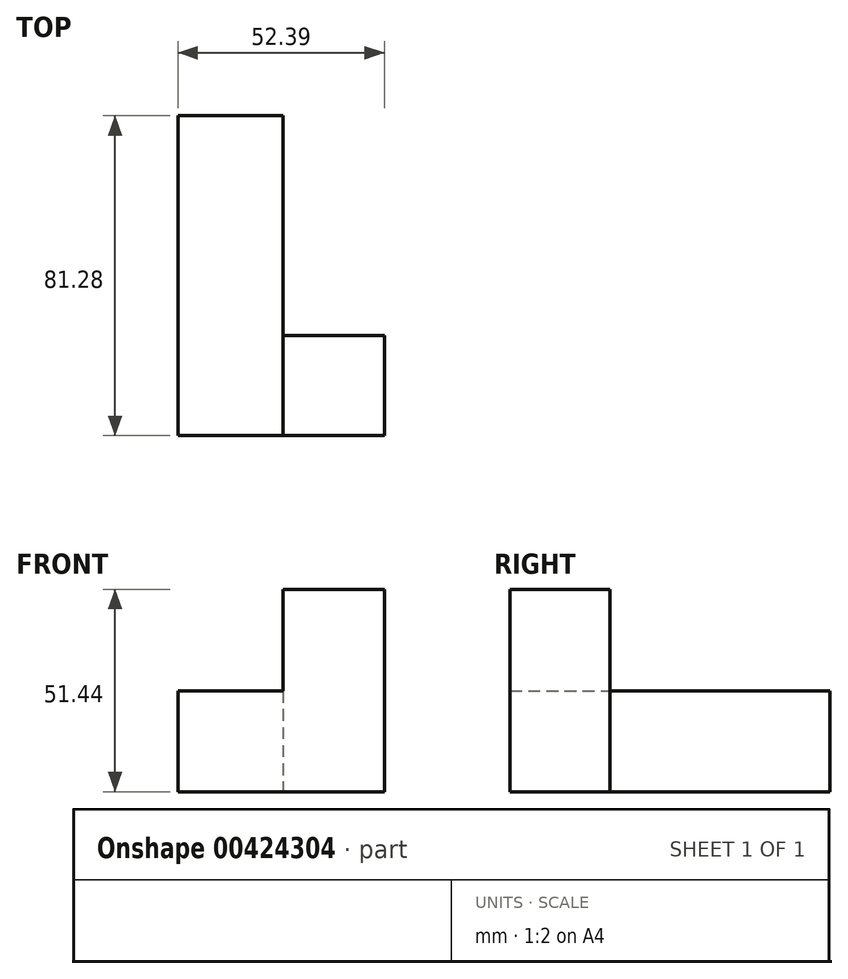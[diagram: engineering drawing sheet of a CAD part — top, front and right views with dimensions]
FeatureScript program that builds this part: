
annotation { "Feature Type Name" : "Feature", "Feature Type Description" : "" }
export const myFeature = defineFeature(function(context is Context, id is Id, definition is map)
    precondition{}
    {
        {
            var Q0;
            Q0=qCreatedBy(makeId("Front.planeOp"),FACE);
            var sketch = newSketch(context, id + "F0", { "sketchPlane" : qUnion([Q0])});
            skLineSegment(sketch, "E0.bottom", {"start": v(0, 0) * mm, "end": v(-25.72, 0) * mm});
            skLineSegment(sketch, "E0.top", {"start": v(0, -25.85) * mm, "end": v(-25.72, -25.85) * mm});
            skLineSegment(sketch, "E0.left", {"start": v(0, 0) * mm, "end": v(0, -25.85) * mm});
            skLineSegment(sketch, "E0.right", {"start": v(-25.72, 0) * mm, "end": v(-25.72, -25.85) * mm});
            skLineSegment(sketch, "E1.top", {"start": v(0, -51.44) * mm, "end": v(-25.72, -51.44) * mm});
            skLineSegment(sketch, "E1.left", {"start": v(0, -25.85) * mm, "end": v(0, -51.44) * mm});
            skLineSegment(sketch, "E1.right", {"start": v(-25.72, -25.85) * mm, "end": v(-25.72, -51.44) * mm});
            skLineSegment(sketch, "E2.bottom", {"start": v(-25.72, -51.44) * mm, "end": v(-52.39, -51.44) * mm});
            skLineSegment(sketch, "E2.top", {"start": v(-25.72, -25.85) * mm, "end": v(-52.39, -25.85) * mm});
            skLineSegment(sketch, "E2.left", {"start": v(-25.72, -51.44) * mm, "end": v(-25.72, -25.85) * mm});
            skLineSegment(sketch, "E2.right", {"start": v(-52.39, -51.44) * mm, "end": v(-52.39, -25.85) * mm});
            skSolve(sketch);
        }
        {
            var Q0;
            Q0=makeQuery(id+"F0.imprint","IMPRINT",FACE,{"disambiguationData":[TD([[makeQuery(id+"F0.imprint","IMPRINT",EDGE,{"derivedFrom":sQuery(id+"F0.wireOp",EDGE,"E0.bottom")}),1.0]])]});
            extrude(context, id + "F1", {"entities" : qUnion([Q0]), "depth" : 25.4 * mm});
        }
        {
            var Q0;
            Q0=makeQuery(id+"F0.imprint","IMPRINT",FACE,{"disambiguationData":[TD([[makeQuery(id+"F0.imprint","IMPRINT",EDGE,{"derivedFrom":sQuery(id+"F0.wireOp",EDGE,"E2.bottom")}),-1.0]])]});
            extrude(context, id + "F2", {"entities" : qUnion([Q0]), "depth" : 25.4 * mm});
        }
        {
            var Q0;
            Q0=makeQuery(id+"F0.imprint","IMPRINT",FACE,{"disambiguationData":[TD([[makeQuery(id+"F0.imprint","IMPRINT",EDGE,{"derivedFrom":sQuery(id+"F0.wireOp",EDGE,"E0.top")}),1.0]])]});
            extrude(context, id + "F3", {"entities" : qUnion([Q0]), "depth" : 25.4 * mm});
        }
        {
            var Q0;
            Q0=makeQuery(id+"F0.imprint","IMPRINT",FACE,{"disambiguationData":[TD([[makeQuery(id+"F0.imprint","IMPRINT",EDGE,{"derivedFrom":sQuery(id+"F0.wireOp",EDGE,"E0.top")}),1.0]])]});
            extrude(context, id + "F4", {"entities" : qUnion([Q0]), "depth" : 25.4 * mm});
        }
        {
            var Q0;
            Q0=makeQuery(id+"F0.imprint","IMPRINT",FACE,{"disambiguationData":[TD([[makeQuery(id+"F0.imprint","IMPRINT",EDGE,{"derivedFrom":sQuery(id+"F0.wireOp",EDGE,"E2.bottom")}),-1.0]])]});
            extrude(context, id + "F5", {"entities" : qUnion([Q0]), "operationType" : NewBodyOperationType.ADD, "oppositeDirection" : true, "depth" : 55.88 * mm});
        }
    });
